# Revit family: Door-Sliding-Kawneer-1010_Mall_Front-OX
name_source: partatom
category: Doors
revit_build: Autodesk Revit 2015 (Build: 20140905_0730(x64)
units: mm (PartAtom-declared; Revit-internal decimal feet)

## types (2) — shared parameters
Appear In Schedule = Yes
Assembly Code = C1020110
CTRL Panel Height = 7' - 10 21/32"
Description = Sliding OX
Frame Depth = 0' - 4 17/32"
Frame Head Width = 0' - 1 3/8"
Frame Jamb Width = 0' - 1"
Function = Interior
Height = 8' - 0"
Intermediate Rail Height = 2' - 6"
Manufacturer = Kawneer
Model = 1010 Sliding Mall Front
Panel Width = 6' - 0 3/32"
Panel Width Fixed = 6' - 0 29/32"
Product Documentation Link = http://www.kawneer.com
Product Page URL = http://www.kawneer.com
Product data url = https://bimobject.com
Shim Space = 0' - 0 1/4"
Thickness = 0' - 1 1/2"
Threshold Height = 0' - 0 19/32"
Threshold Material = Aluminum - Kawneer - Clear
URL = http://www.kawneer.com
Wall Closure = By host
Width = 12' - 0"

## per-type parameters (varying)
| type | Glazing Thickness | Type Comments |
| 12'x8' - 1/4" Glazing | 0' - 0 1/4" | 1/4" Glazing |
| 12'x8' - 1" Glazing | 0' - 1" | 1" Glazing |

## geometry (parser evidence)
native form markers: Blend x10, Sweep x4
no freeform markers — native parametric forms only
